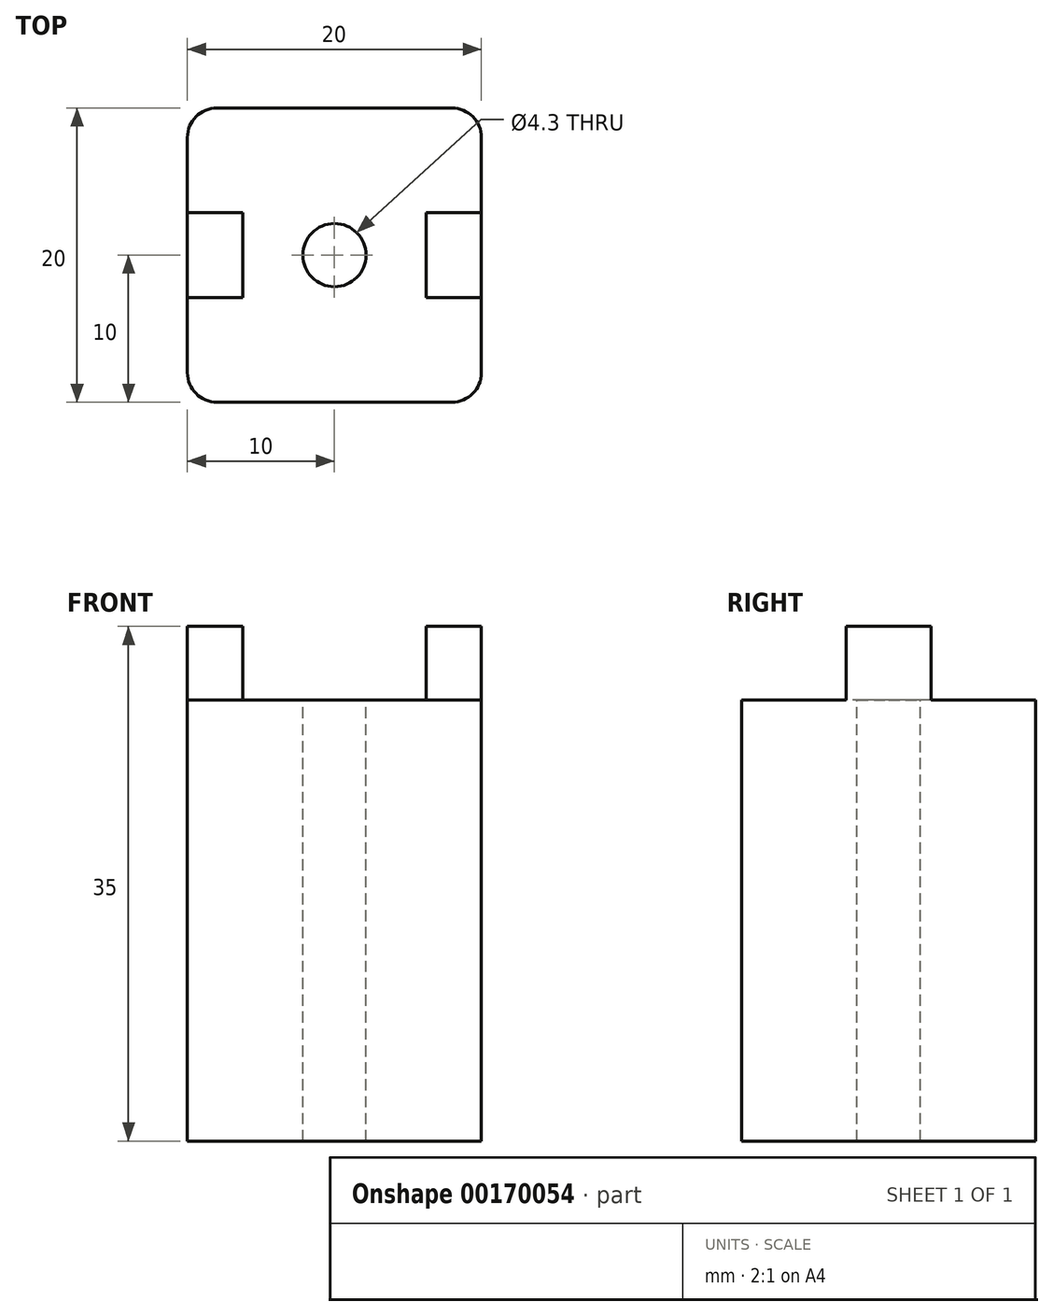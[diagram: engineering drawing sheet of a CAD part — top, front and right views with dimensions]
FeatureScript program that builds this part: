
annotation { "Feature Type Name" : "Feature", "Feature Type Description" : "" }
export const myFeature = defineFeature(function(context is Context, id is Id, definition is map)
    precondition{}
    {
        {
            var Q0;
            Q0=qCreatedBy(makeId("Top.planeOp"),FACE);
            var sketch = newSketch(context, id + "F0", { "sketchPlane" : qUnion([Q0])});
            skLineSegment(sketch, "E0.bottom", {"start": v(0, 0) * mm, "end": v(20, 0) * mm});
            skLineSegment(sketch, "E0.top", {"start": v(0, 20) * mm, "end": v(20, 20) * mm});
            skLineSegment(sketch, "E0.left", {"start": v(0, 0) * mm, "end": v(0, 20) * mm});
            skLineSegment(sketch, "E0.right", {"start": v(20, 0) * mm, "end": v(20, 20) * mm});
            skSolve(sketch);
        }
        {
            var Q0;
            Q0=makeQuery(id+"F0.imprint","IMPRINT",FACE,{"disambiguationData":[TD([[makeQuery(id+"F0.imprint","IMPRINT",EDGE,{"derivedFrom":sQuery(id+"F0.wireOp",EDGE,"E0.bottom")}),1.0]])]});
            extrude(context, id + "F1", {"entities" : qUnion([Q0]), "depth" : 30 * mm});
        }
        {
            var Q0;
            Q0=makeQuery(id+"F1.opExtrude","CAP_FACE",FACE,{"disambiguationData":[OSD([sQuery(id+"F0.wireOp",EDGE,"E0.bottom"),sQuery(id+"F0.wireOp",EDGE,"E0.top"),sQuery(id+"F0.wireOp",EDGE,"E0.left"),sQuery(id+"F0.wireOp",EDGE,"E0.right")])],"isStart":false});
            var sketch = newSketch(context, id + "F2", { "sketchPlane" : qUnion([Q0])});
            skCircle(sketch, "E1", {"center": v(10, 10) * mm, "radius": 2.15 * mm});
            skPoint(sketch, "E1.centerSnap0", {"position": v(0, 10) * mm});
            skPoint(sketch, "E1.centerSnap1", {"position": v(10, 0) * mm});
            skSolve(sketch);
        }
        {
            var Q0;
            Q0=makeQuery(id+"F2.imprint","IMPRINT",FACE,{"disambiguationData":[TD([[makeQuery(id+"F2.imprint","IMPRINT",EDGE,{"derivedFrom":sQuery(id+"F2.wireOp",EDGE,"E1")}),1.0]])]});
            extrude(context, id + "F3", {"entities" : qUnion([Q0]), "operationType" : NewBodyOperationType.REMOVE, "endBound" : BoundingType.THROUGH_ALL, "oppositeDirection" : true, "depth" : 25 * mm});
        }
        {
            var Q0;
            Q0=makeQuery(id+"F1.opExtrude","SWEPT_EDGE",EDGE,{"disambiguationData":[OSD([sQuery(id+"F0.wireOp",EDGE,"E0.bottom"),sQuery(id+"F0.wireOp",EDGE,"E0.right")])]});
            var Q1;
            Q1=makeQuery(id+"F1.opExtrude","SWEPT_EDGE",EDGE,{"disambiguationData":[OSD([sQuery(id+"F0.wireOp",EDGE,"E0.bottom"),sQuery(id+"F0.wireOp",EDGE,"E0.left")])]});
            var Q2;
            Q2=makeQuery(id+"F1.opExtrude","SWEPT_EDGE",EDGE,{"disambiguationData":[OSD([sQuery(id+"F0.wireOp",EDGE,"E0.top"),sQuery(id+"F0.wireOp",EDGE,"E0.right")])]});
            var Q3;
            Q3=makeQuery(id+"F1.opExtrude","SWEPT_EDGE",EDGE,{"disambiguationData":[OSD([sQuery(id+"F0.wireOp",EDGE,"E0.top"),sQuery(id+"F0.wireOp",EDGE,"E0.left")])]});
            fillet(context, id + "F4", {"entities" : qUnion([Q0, Q1, Q2, Q3]), "radius" : 2 * mm, "tangentPropagation" : true, "allowEdgeOverflow" : false});
        }
        {
            var Q0;
            Q0=makeQuery(id+"F1.opExtrude","CAP_FACE",FACE,{"disambiguationData":[OSD([sQuery(id+"F0.wireOp",EDGE,"E0.bottom"),sQuery(id+"F0.wireOp",EDGE,"E0.top"),sQuery(id+"F0.wireOp",EDGE,"E0.left"),sQuery(id+"F0.wireOp",EDGE,"E0.right")])],"isStart":false});
            var sketch = newSketch(context, id + "F5", { "sketchPlane" : qUnion([Q0])});
            skLineSegment(sketch, "E2.bottom", {"start": v(0, 7.1) * mm, "end": v(3.75, 7.1) * mm});
            skLineSegment(sketch, "E2.top", {"start": v(0, 12.9) * mm, "end": v(3.75, 12.9) * mm});
            skLineSegment(sketch, "E2.left", {"start": v(0, 7.1) * mm, "end": v(0, 12.9) * mm});
            skLineSegment(sketch, "E2.right", {"start": v(3.75, 7.1) * mm, "end": v(3.75, 12.9) * mm});
            skLineSegment(sketch, "E3.bottom", {"start": v(16.25, 12.9) * mm, "end": v(20, 12.9) * mm});
            skLineSegment(sketch, "E3.top", {"start": v(16.25, 7.1) * mm, "end": v(20, 7.1) * mm});
            skLineSegment(sketch, "E3.left", {"start": v(16.25, 12.9) * mm, "end": v(16.25, 7.1) * mm});
            skLineSegment(sketch, "E3.right", {"start": v(20, 12.9) * mm, "end": v(20, 7.1) * mm});
            skSolve(sketch);
        }
        {
            var Q0;
            Q0=makeQuery(id+"F5.imprint","IMPRINT",FACE,{"disambiguationData":[TD([[makeQuery(id+"F5.imprint","IMPRINT",EDGE,{"derivedFrom":sQuery(id+"F5.wireOp",EDGE,"E2.bottom")}),1.0]])]});
            var Q1;
            Q1=makeQuery(id+"F5.imprint","IMPRINT",FACE,{"disambiguationData":[TD([[makeQuery(id+"F5.imprint","IMPRINT",EDGE,{"derivedFrom":sQuery(id+"F5.wireOp",EDGE,"E3.bottom")}),-1.0]])]});
            extrude(context, id + "F6", {"entities" : qUnion([Q0, Q1]), "operationType" : NewBodyOperationType.ADD, "depth" : 5 * mm});
        }
    });
